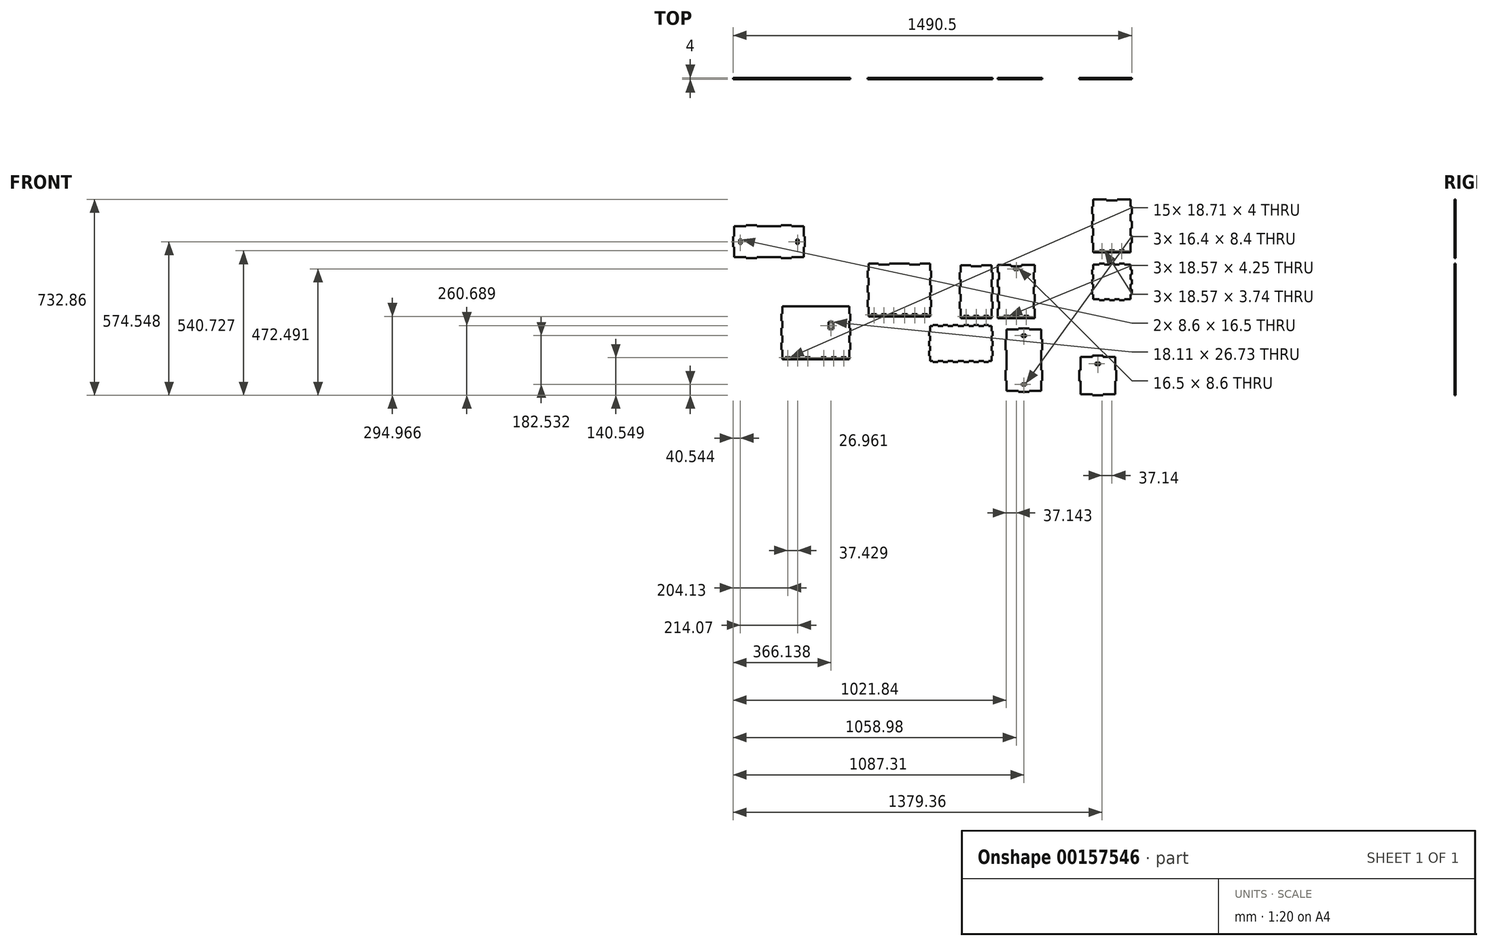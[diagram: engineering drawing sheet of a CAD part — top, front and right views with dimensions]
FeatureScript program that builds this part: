
annotation { "Feature Type Name" : "Feature", "Feature Type Description" : "" }
export const myFeature = defineFeature(function(context is Context, id is Id, definition is map)
    precondition{}
    {
        {
            var Q0;
            Q0=qCreatedBy(makeId("Front.planeOp"),FACE);
            var sketch = newSketch(context, id + "F0", { "sketchPlane" : qUnion([Q0])});
            skLineSegment(sketch, "E0.top", {"start": v(-322.76, -104.52) * mm, "end": v(-304.05, -104.52) * mm});
            skPoint(sketch, "E1.orphan", {"position": v(-191.3, 92.98) * mm});
            skLineSegment(sketch, "E2.0", {"start": v(-322.76, -108.52) * mm, "end": v(-304.05, -108.52) * mm});
            skLineSegment(sketch, "E3.2.0.0", {"start": v(-304.05, -104.52) * mm, "end": v(-304.05, -108.52) * mm});
            skLineSegment(sketch, "E3.3.0.0", {"start": v(-285.34, -104.52) * mm, "end": v(-285.34, -108.52) * mm});
            skLineSegment(sketch, "E3.4.0.0", {"start": v(-266.62, -104.52) * mm, "end": v(-266.62, -108.52) * mm});
            skLineSegment(sketch, "E3.5.0.0", {"start": v(-247.9, -104.52) * mm, "end": v(-247.9, -108.52) * mm});
            skLineSegment(sketch, "E3.6.0.0", {"start": v(-229.2, -104.52) * mm, "end": v(-229.2, -108.52) * mm});
            skLineSegment(sketch, "E4.trimOffspring", {"start": v(-285.34, -104.52) * mm, "end": v(-266.62, -104.52) * mm});
            skLineSegment(sketch, "E5.trimOffspring", {"start": v(-285.34, -108.52) * mm, "end": v(-266.62, -108.52) * mm});
            skLineSegment(sketch, "E6.trimOffspring", {"start": v(-247.9, -104.52) * mm, "end": v(-229.2, -104.52) * mm});
            skLineSegment(sketch, "E7.trimOffspring", {"start": v(-247.9, -108.52) * mm, "end": v(-229.2, -108.52) * mm});
            skLineSegment(sketch, "E8", {"start": v(-322.76, -108.52) * mm, "end": v(-322.76, -104.52) * mm});
            skLineSegment(sketch, "E9.1.0.0", {"start": v(-172.4, -104.27) * mm, "end": v(-172.4, -108.52) * mm});
            skLineSegment(sketch, "E9.2.0.0", {"start": v(-153.84, -104.27) * mm, "end": v(-153.84, -108.52) * mm});
            skLineSegment(sketch, "E9.3.0.0", {"start": v(-135.27, -104.27) * mm, "end": v(-135.27, -108.52) * mm});
            skLineSegment(sketch, "E9.4.0.0", {"start": v(-116.7, -104.27) * mm, "end": v(-116.7, -108.52) * mm});
            skLineSegment(sketch, "E9.5.0.0", {"start": v(-98.12, -104.27) * mm, "end": v(-98.12, -108.52) * mm});
            skLineSegment(sketch, "E9.6.0.0", {"start": v(-79.55, -104.27) * mm, "end": v(-79.55, -108.52) * mm});
            skLineSegment(sketch, "E10", {"start": v(-172.4, -108.52) * mm, "end": v(-153.84, -108.52) * mm});
            skLineSegment(sketch, "E11", {"start": v(-172.4, -104.27) * mm, "end": v(-153.84, -104.27) * mm});
            skPoint(sketch, "E12.orphan", {"position": v(-190.98, -108.52) * mm});
            skLineSegment(sketch, "E13.trimOffspring", {"start": v(-135.27, -104.27) * mm, "end": v(-116.7, -104.27) * mm});
            skLineSegment(sketch, "E14.trimOffspring", {"start": v(-135.27, -108.52) * mm, "end": v(-116.7, -108.52) * mm});
            skLineSegment(sketch, "E15.trimOffspring", {"start": v(-98.12, -104.27) * mm, "end": v(-79.55, -104.27) * mm});
            skLineSegment(sketch, "E16.trimOffspring", {"start": v(-98.12, -108.52) * mm, "end": v(-79.55, -108.52) * mm});
            skPoint(sketch, "E17.orphan", {"position": v(-190.98, -104.27) * mm});
            skPoint(sketch, "E18.orphan", {"position": v(-153.84, -112.52) * mm});
            skPoint(sketch, "E19.orphan", {"position": v(-135.27, -112.52) * mm});
            skPoint(sketch, "E20.orphan", {"position": v(-116.7, -112.52) * mm});
            skPoint(sketch, "E21.orphan", {"position": v(-98.12, -112.52) * mm});
            skPoint(sketch, "E22.orphan", {"position": v(-79.55, -112.52) * mm});
            skLineSegment(sketch, "E23.top", {"start": v(-322.76, -138.52) * mm, "end": v(-304.05, -138.52) * mm});
            skLineSegment(sketch, "E24.2.0.0", {"start": v(-304.05, -138.52) * mm, "end": v(-304.05, -142.52) * mm});
            skLineSegment(sketch, "E24.3.0.0", {"start": v(-285.34, -138.52) * mm, "end": v(-285.34, -142.52) * mm});
            skLineSegment(sketch, "E24.4.0.0", {"start": v(-266.62, -138.52) * mm, "end": v(-266.62, -142.52) * mm});
            skLineSegment(sketch, "E24.5.0.0", {"start": v(-247.9, -138.52) * mm, "end": v(-247.9, -142.52) * mm});
            skLineSegment(sketch, "E24.6.0.0", {"start": v(-229.2, -138.52) * mm, "end": v(-229.2, -142.52) * mm});
            skLineSegment(sketch, "E25.trimOffspring", {"start": v(-285.34, -138.52) * mm, "end": v(-266.62, -138.52) * mm});
            skLineSegment(sketch, "E26.trimOffspring", {"start": v(-247.9, -138.52) * mm, "end": v(-229.2, -138.52) * mm});
            skLineSegment(sketch, "E27", {"start": v(-322.76, -142.52) * mm, "end": v(-322.76, -138.52) * mm});
            skLineSegment(sketch, "E28", {"start": v(-304.05, -142.52) * mm, "end": v(-285.34, -142.52) * mm});
            skLineSegment(sketch, "E29", {"start": v(-266.62, -142.52) * mm, "end": v(-247.9, -142.52) * mm});
            skLineSegment(sketch, "E30", {"start": v(-229.2, -142.52) * mm, "end": v(-218.48, -142.4) * mm});
            skLineSegment(sketch, "E31", {"start": v(-322.76, -142.52) * mm, "end": v(-333.48, -142.52) * mm});
            skPoint(sketch, "E32.orphan", {"position": v(-210.48, -131.68) * mm});
            skLineSegment(sketch, "E33", {"start": v(-218.48, -142.4) * mm, "end": v(-218.48, -161.1) * mm});
            skLineSegment(sketch, "E34.MirrorCS", {"start": v(-266.62, -276.52) * mm, "end": v(-266.62, -272.52) * mm});
            skLineSegment(sketch, "E35.MirrorCS", {"start": v(-247.9, -276.52) * mm, "end": v(-247.9, -272.52) * mm});
            skLineSegment(sketch, "E36.MirrorCS", {"start": v(-229.2, -276.52) * mm, "end": v(-229.2, -272.52) * mm});
            skLineSegment(sketch, "E37.MirrorCS", {"start": v(-322.76, -272.52) * mm, "end": v(-322.76, -276.52) * mm});
            skLineSegment(sketch, "E38.MirrorCS", {"start": v(-285.34, -276.52) * mm, "end": v(-285.34, -272.52) * mm});
            skLineSegment(sketch, "E39.MirrorCS", {"start": v(-304.05, -276.52) * mm, "end": v(-304.05, -272.52) * mm});
            skLineSegment(sketch, "E40.MirrorCS", {"start": v(-322.76, -272.52) * mm, "end": v(-333.48, -272.52) * mm});
            skLineSegment(sketch, "E41.MirrorCS", {"start": v(-285.34, -276.52) * mm, "end": v(-266.62, -276.52) * mm});
            skPoint(sketch, "E42.MirrorP", {"position": v(-210.48, -283.36) * mm});
            skLineSegment(sketch, "E43.MirrorCS", {"start": v(-247.9, -276.52) * mm, "end": v(-229.2, -276.52) * mm});
            skLineSegment(sketch, "E44.MirrorCS", {"start": v(-322.76, -276.52) * mm, "end": v(-304.05, -276.52) * mm});
            skLineSegment(sketch, "E45.MirrorCS", {"start": v(-266.62, -272.52) * mm, "end": v(-247.9, -272.52) * mm});
            skLineSegment(sketch, "E46.MirrorCS", {"start": v(-304.05, -272.52) * mm, "end": v(-285.34, -272.52) * mm});
            skPoint(sketch, "E47.orphan", {"position": v(-218.48, -129.29) * mm});
            skPoint(sketch, "E48.orphan", {"position": v(-210.48, -142.32) * mm});
            skLineSegment(sketch, "E49", {"start": v(-218.48, -161.1) * mm, "end": v(-214.48, -161.1) * mm});
            skLineSegment(sketch, "E50", {"start": v(-229.2, -272.52) * mm, "end": v(-218.48, -272.63) * mm});
            skLineSegment(sketch, "E51.1.0.0", {"start": v(-337.64, 58.34) * mm, "end": v(-333.64, 58.34) * mm});
            skLineSegment(sketch, "E51.2.0.0", {"start": v(-337.64, 31.2) * mm, "end": v(-333.64, 31.2) * mm});
            skLineSegment(sketch, "E51.3.0.0", {"start": v(-337.64, 4.06) * mm, "end": v(-333.64, 4.06) * mm});
            skLineSegment(sketch, "E51.4.0.0", {"start": v(-337.64, -23.09) * mm, "end": v(-333.64, -23.09) * mm});
            skLineSegment(sketch, "E51.5.0.0", {"start": v(-337.64, -50.23) * mm, "end": v(-333.64, -50.23) * mm});
            skLineSegment(sketch, "E51.6.0.0", {"start": v(-337.64, -77.37) * mm, "end": v(-333.64, -77.37) * mm});
            skLineSegment(sketch, "E52", {"start": v(-195.52, 58.34) * mm, "end": v(-190.98, 58.34) * mm});
            skPoint(sketch, "E53.endSnap0", {"position": v(-163.12, -104.27) * mm});
            skLineSegment(sketch, "E54.left", {"start": v(-190.98, 58.34) * mm, "end": v(-190.98, 31.2) * mm});
            skLineSegment(sketch, "E55", {"start": v(-195.52, 85.73) * mm, "end": v(-195.52, 58.34) * mm});
            skLineSegment(sketch, "E56.trimOffspring", {"start": v(-195.52, 31.2) * mm, "end": v(-195.52, 4.06) * mm});
            skLineSegment(sketch, "E57.trimOffspring", {"start": v(-195.52, -23.09) * mm, "end": v(-195.52, -50.23) * mm});
            skLineSegment(sketch, "E58.trimOffspring", {"start": v(-195.52, 4.06) * mm, "end": v(-190.98, 4.06) * mm});
            skLineSegment(sketch, "E59.trimOffspring", {"start": v(-195.52, 31.2) * mm, "end": v(-190.98, 31.2) * mm});
            skLineSegment(sketch, "E60.trimOffspring", {"start": v(-195.52, -23.09) * mm, "end": v(-190.98, -23.09) * mm});
            skLineSegment(sketch, "E61.trimOffspring", {"start": v(-195.52, -50.23) * mm, "end": v(-190.98, -50.23) * mm});
            skLineSegment(sketch, "E62.trimOffspring", {"start": v(-195.52, -77.37) * mm, "end": v(-190.98, -77.37) * mm});
            skLineSegment(sketch, "E63.trimOffspring", {"start": v(-195.52, -77.37) * mm, "end": v(-195.52, -112.52) * mm});
            skLineSegment(sketch, "E64", {"start": v(-190.98, -104.27) * mm, "end": v(-190.98, -104.44) * mm});
            skPoint(sketch, "E65.orphan", {"position": v(-180.53, -104.27) * mm});
            skLineSegment(sketch, "E66.trimOffspring", {"start": v(-190.98, 4.06) * mm, "end": v(-190.98, -23.09) * mm});
            skLineSegment(sketch, "E67.trimOffspring", {"start": v(-190.98, -50.23) * mm, "end": v(-190.98, -77.37) * mm});
            skLineSegment(sketch, "E68.0", {"start": v(-333.64, 85.48) * mm, "end": v(-333.64, 58.34) * mm});
            skLineSegment(sketch, "E69.trimOffspring", {"start": v(-333.64, 31.2) * mm, "end": v(-333.64, 4.06) * mm});
            skLineSegment(sketch, "E70.trimOffspring", {"start": v(-333.64, 85.48) * mm, "end": v(-296.14, 85.48) * mm});
            skLineSegment(sketch, "E71.trimOffspring", {"start": v(-333.64, -23.09) * mm, "end": v(-333.64, -50.23) * mm});
            skLineSegment(sketch, "E72.trimOffspring", {"start": v(-333.64, -77.37) * mm, "end": v(-333.64, -112.52) * mm});
            skLineSegment(sketch, "E73.trimOffspring", {"start": v(-333.64, -112.52) * mm, "end": v(-218.64, -112.52) * mm});
            skLineSegment(sketch, "E74", {"start": v(-337.64, -77.37) * mm, "end": v(-337.64, -50.23) * mm});
            skLineSegment(sketch, "E75", {"start": v(-337.64, -23.09) * mm, "end": v(-337.64, 4.06) * mm});
            skLineSegment(sketch, "E76", {"start": v(-337.64, 31.2) * mm, "end": v(-337.64, 58.34) * mm});
            skLineSegment(sketch, "E77.MirrorCS", {"start": v(-214.64, 58.34) * mm, "end": v(-218.64, 58.34) * mm});
            skLineSegment(sketch, "E78.MirrorCS", {"start": v(-214.64, -50.23) * mm, "end": v(-218.64, -50.23) * mm});
            skLineSegment(sketch, "E79.MirrorCS", {"start": v(-214.64, 31.2) * mm, "end": v(-218.64, 31.2) * mm});
            skLineSegment(sketch, "E80.MirrorCS", {"start": v(-214.64, -77.37) * mm, "end": v(-218.64, -77.37) * mm});
            skLineSegment(sketch, "E81.MirrorCS", {"start": v(-214.64, -23.09) * mm, "end": v(-218.64, -23.09) * mm});
            skLineSegment(sketch, "E82.MirrorCS", {"start": v(-214.64, 4.06) * mm, "end": v(-218.64, 4.06) * mm});
            skPoint(sketch, "E83.MirrorP", {"position": v(-211.02, 4.06) * mm});
            skLineSegment(sketch, "E84.MirrorCS", {"start": v(-214.64, -23.09) * mm, "end": v(-214.64, 4.06) * mm});
            skLineSegment(sketch, "E85.MirrorCS", {"start": v(-214.64, -77.37) * mm, "end": v(-214.64, -50.23) * mm});
            skLineSegment(sketch, "E86.MirrorCS", {"start": v(-218.64, -77.37) * mm, "end": v(-218.64, -112.52) * mm});
            skLineSegment(sketch, "E87.MirrorCS", {"start": v(-218.64, -23.09) * mm, "end": v(-218.64, -50.23) * mm});
            skLineSegment(sketch, "E88.MirrorCS", {"start": v(-214.64, 31.2) * mm, "end": v(-214.64, 58.34) * mm});
            skPoint(sketch, "E89.MirrorP", {"position": v(-211.56, -77.37) * mm});
            skPoint(sketch, "E90.MirrorP", {"position": v(-211.38, -50.23) * mm});
            skPoint(sketch, "E91.MirrorP", {"position": v(-211.2, -23.09) * mm});
            skLineSegment(sketch, "E92.MirrorCS", {"start": v(-218.64, 31.2) * mm, "end": v(-218.64, 4.06) * mm});
            skLineSegment(sketch, "E93.MirrorCS", {"start": v(-218.64, 85.48) * mm, "end": v(-218.64, 58.34) * mm});
            skPoint(sketch, "E94.MirrorP", {"position": v(-210.84, 31.2) * mm});
            skPoint(sketch, "E95.orphan", {"position": v(-210.64, -112.52) * mm});
            skPoint(sketch, "E96.MirrorP", {"position": v(-75.98, -104.27) * mm});
            skLineSegment(sketch, "E97.1.0.0", {"start": v(-218.48, -179.67) * mm, "end": v(-214.48, -179.67) * mm});
            skLineSegment(sketch, "E97.2.0.0", {"start": v(-218.48, -198.24) * mm, "end": v(-214.48, -198.24) * mm});
            skLineSegment(sketch, "E97.3.0.0", {"start": v(-218.48, -216.8) * mm, "end": v(-214.48, -216.81) * mm});
            skLineSegment(sketch, "E97.4.0.0", {"start": v(-218.48, -235.38) * mm, "end": v(-214.48, -235.38) * mm});
            skLineSegment(sketch, "E97.5.0.0", {"start": v(-218.48, -253.95) * mm, "end": v(-214.48, -253.95) * mm});
            skLineSegment(sketch, "E97.6.0.0", {"start": v(-229.99, -272.52) * mm, "end": v(-218.48, -272.52) * mm, "construction": true});
            skLineSegment(sketch, "E98", {"start": v(-214.48, -161.1) * mm, "end": v(-214.48, -179.67) * mm});
            skLineSegment(sketch, "E99.trimOffspring", {"start": v(-214.48, -198.24) * mm, "end": v(-214.48, -216.81) * mm});
            skLineSegment(sketch, "E100.trimOffspring", {"start": v(-214.48, -235.38) * mm, "end": v(-214.48, -253.95) * mm});
            skPoint(sketch, "E101.orphan", {"position": v(-190.56, -272.54) * mm});
            skLineSegment(sketch, "E102.trimOffspring", {"start": v(-218.48, -179.67) * mm, "end": v(-218.48, -198.24) * mm});
            skLineSegment(sketch, "E103.trimOffspring", {"start": v(-218.48, -216.8) * mm, "end": v(-218.48, -235.38) * mm});
            skLineSegment(sketch, "E104.trimOffspring", {"start": v(-218.48, -253.95) * mm, "end": v(-218.48, -272.63) * mm});
            skPoint(sketch, "E105.orphan", {"position": v(-229.73, -235.37) * mm});
            skPoint(sketch, "E106.orphan", {"position": v(-229.86, -253.94) * mm});
            skPoint(sketch, "E107.orphan", {"position": v(-229.6, -216.8) * mm});
            skPoint(sketch, "E108.orphan", {"position": v(-229.46, -198.23) * mm});
            skPoint(sketch, "E109.orphan", {"position": v(-189.78, -161.11) * mm});
            skPoint(sketch, "E110.orphan", {"position": v(-189.91, -179.68) * mm});
            skPoint(sketch, "E111.orphan", {"position": v(-190.04, -198.26) * mm});
            skPoint(sketch, "E112.orphan", {"position": v(-190.17, -216.83) * mm});
            skPoint(sketch, "E113.orphan", {"position": v(-190.3, -235.4) * mm});
            skPoint(sketch, "E114.orphan", {"position": v(-190.43, -253.97) * mm});
            skPoint(sketch, "E115.MirrorP", {"position": v(-341.48, -142.32) * mm});
            skPoint(sketch, "E116.MirrorP", {"position": v(-341.48, -283.36) * mm});
            skPoint(sketch, "E117.MirrorP", {"position": v(-341.48, -131.68) * mm});
            skPoint(sketch, "E118.MirrorP", {"position": v(-333.48, -129.29) * mm});
            skLineSegment(sketch, "E119.MirrorCS", {"start": v(-60.98, -104.27) * mm, "end": v(-60.98, -104.44) * mm});
            skLineSegment(sketch, "E120.MirrorCS", {"start": v(-56.44, 31.2) * mm, "end": v(-60.98, 31.2) * mm});
            skLineSegment(sketch, "E121.MirrorCS", {"start": v(-56.44, -77.37) * mm, "end": v(-60.98, -77.37) * mm});
            skLineSegment(sketch, "E122.MirrorCS", {"start": v(-56.44, -23.09) * mm, "end": v(-60.98, -23.09) * mm});
            skLineSegment(sketch, "E123.MirrorCS", {"start": v(-56.44, 58.34) * mm, "end": v(-60.98, 58.34) * mm});
            skLineSegment(sketch, "E124.MirrorCS", {"start": v(-56.44, 4.06) * mm, "end": v(-60.98, 4.06) * mm});
            skLineSegment(sketch, "E125.MirrorCS", {"start": v(-56.44, -50.23) * mm, "end": v(-60.98, -50.23) * mm});
            skPoint(sketch, "E126.MirrorP", {"position": v(-60.98, 92.98) * mm});
            skLineSegment(sketch, "E127.MirrorCS", {"start": v(-56.44, -77.37) * mm, "end": v(-56.44, -112.52) * mm});
            skPoint(sketch, "E128.MirrorP", {"position": v(-60.98, -108.52) * mm});
            skPoint(sketch, "E129.MirrorP", {"position": v(-60.98, -104.27) * mm});
            skLineSegment(sketch, "E130.MirrorCS", {"start": v(-60.98, 4.06) * mm, "end": v(-60.98, -23.09) * mm});
            skPoint(sketch, "E131.MirrorP", {"position": v(-71.43, -104.27) * mm});
            skLineSegment(sketch, "E132.MirrorCS", {"start": v(-60.98, -50.23) * mm, "end": v(-60.98, -77.37) * mm});
            skLineSegment(sketch, "E133.MirrorCS", {"start": v(-60.98, 58.34) * mm, "end": v(-60.98, 31.2) * mm});
            skLineSegment(sketch, "E134.MirrorCS", {"start": v(-56.44, 31.2) * mm, "end": v(-56.44, 4.06) * mm});
            skLineSegment(sketch, "E135.MirrorCS", {"start": v(-56.44, -23.09) * mm, "end": v(-56.44, -50.23) * mm});
            skLineSegment(sketch, "E136.MirrorCS", {"start": v(-56.44, 85.73) * mm, "end": v(-56.44, 58.34) * mm});
            skLineSegment(sketch, "E137", {"start": v(-195.52, 85.73) * mm, "end": v(-145.98, 85.73) * mm});
            skLineSegment(sketch, "E138", {"start": v(-195.52, -112.52) * mm, "end": v(-56.44, -112.52) * mm});
            skLineSegment(sketch, "E139.top", {"start": v(-296.14, 81.48) * mm, "end": v(-256.14, 81.48) * mm});
            skLineSegment(sketch, "E139.left", {"start": v(-296.14, 85.48) * mm, "end": v(-296.14, 81.48) * mm});
            skLineSegment(sketch, "E139.right", {"start": v(-256.14, 85.48) * mm, "end": v(-256.14, 81.48) * mm});
            skLineSegment(sketch, "E140.top", {"start": v(-145.98, 81.73) * mm, "end": v(-105.98, 81.73) * mm});
            skLineSegment(sketch, "E140.left", {"start": v(-145.98, 85.73) * mm, "end": v(-145.98, 81.73) * mm});
            skLineSegment(sketch, "E140.right", {"start": v(-105.98, 85.73) * mm, "end": v(-105.98, 81.73) * mm});
            skLineSegment(sketch, "E141.trimOffspring", {"start": v(-256.14, 85.48) * mm, "end": v(-218.64, 85.48) * mm});
            skPoint(sketch, "E142.orphan", {"position": v(-296.14, 92.98) * mm});
            skLineSegment(sketch, "E143.trimOffspring", {"start": v(-105.98, 85.73) * mm, "end": v(-56.44, 85.73) * mm});
            skLineSegment(sketch, "E144.bottom", {"start": v(-162.65, -154.55) * mm, "end": v(-117.65, -154.55) * mm});
            skLineSegment(sketch, "E144.left", {"start": v(-162.65, -154.55) * mm, "end": v(-162.65, -192.05) * mm});
            skLineSegment(sketch, "E144.right", {"start": v(-32.65, -154.55) * mm, "end": v(-32.65, -192.05) * mm});
            skLineSegment(sketch, "E145.bottom", {"start": v(-162.65, -192.05) * mm, "end": v(-166.65, -192.05) * mm});
            skLineSegment(sketch, "E145.top", {"start": v(-162.65, -232.05) * mm, "end": v(-166.65, -232.05) * mm});
            skLineSegment(sketch, "E145.right", {"start": v(-166.65, -192.05) * mm, "end": v(-166.65, -232.05) * mm});
            skLineSegment(sketch, "E146.bottom", {"start": v(-117.65, -150.55) * mm, "end": v(-77.65, -150.55) * mm});
            skLineSegment(sketch, "E146.left", {"start": v(-117.65, -150.55) * mm, "end": v(-117.65, -154.55) * mm});
            skLineSegment(sketch, "E146.right", {"start": v(-77.65, -150.55) * mm, "end": v(-77.65, -154.55) * mm});
            skLineSegment(sketch, "E147.trimOffspring", {"start": v(-162.65, -232.05) * mm, "end": v(-162.65, -269.55) * mm});
            skLineSegment(sketch, "E148.trimOffspring", {"start": v(-77.65, -154.55) * mm, "end": v(-32.65, -154.55) * mm});
            skLineSegment(sketch, "E149.MirrorCS", {"start": v(-32.65, -232.05) * mm, "end": v(-28.65, -232.05) * mm});
            skLineSegment(sketch, "E150.MirrorCS", {"start": v(-28.65, -192.05) * mm, "end": v(-28.65, -232.05) * mm});
            skLineSegment(sketch, "E151.MirrorCS", {"start": v(-32.65, -192.05) * mm, "end": v(-28.65, -192.05) * mm});
            skLineSegment(sketch, "E152.trimOffspring", {"start": v(-32.65, -232.05) * mm, "end": v(-32.65, -269.55) * mm});
            skLineSegment(sketch, "E153.MirrorCS", {"start": v(-437.76, -142.52) * mm, "end": v(-448.48, -142.4) * mm});
            skLineSegment(sketch, "E154.MirrorCS", {"start": v(-362.9, -138.52) * mm, "end": v(-362.9, -142.52) * mm});
            skLineSegment(sketch, "E155.MirrorCS", {"start": v(-437.76, -138.52) * mm, "end": v(-437.76, -142.52) * mm});
            skLineSegment(sketch, "E156.MirrorCS", {"start": v(-381.62, -138.52) * mm, "end": v(-381.62, -142.52) * mm});
            skLineSegment(sketch, "E157.MirrorCS", {"start": v(-400.34, -138.52) * mm, "end": v(-400.34, -142.52) * mm});
            skLineSegment(sketch, "E158.MirrorCS", {"start": v(-419.05, -138.52) * mm, "end": v(-419.05, -142.52) * mm});
            skLineSegment(sketch, "E159.MirrorCS", {"start": v(-344.2, -142.52) * mm, "end": v(-344.2, -138.52) * mm});
            skLineSegment(sketch, "E160.MirrorCS", {"start": v(-362.9, -142.52) * mm, "end": v(-381.62, -142.52) * mm});
            skPoint(sketch, "E161.MirrorP", {"position": v(-456.48, -142.32) * mm});
            skLineSegment(sketch, "E162.MirrorCS", {"start": v(-400.34, -142.52) * mm, "end": v(-419.05, -142.52) * mm});
            skLineSegment(sketch, "E163.MirrorCS", {"start": v(-419.05, -138.52) * mm, "end": v(-437.76, -138.52) * mm});
            skPoint(sketch, "E164.MirrorP", {"position": v(-456.48, -131.68) * mm});
            skLineSegment(sketch, "E165.MirrorCS", {"start": v(-344.2, -138.52) * mm, "end": v(-362.9, -138.52) * mm});
            skLineSegment(sketch, "E166.MirrorCS", {"start": v(-381.62, -138.52) * mm, "end": v(-400.34, -138.52) * mm});
            skLineSegment(sketch, "E167.MirrorCS", {"start": v(-437.76, -276.52) * mm, "end": v(-437.76, -272.52) * mm});
            skLineSegment(sketch, "E168.MirrorCS", {"start": v(-344.2, -272.52) * mm, "end": v(-344.2, -276.52) * mm});
            skLineSegment(sketch, "E169.MirrorCS", {"start": v(-419.05, -276.52) * mm, "end": v(-419.05, -272.52) * mm});
            skLineSegment(sketch, "E170.MirrorCS", {"start": v(-400.34, -276.52) * mm, "end": v(-400.34, -272.52) * mm});
            skLineSegment(sketch, "E171.MirrorCS", {"start": v(-381.62, -276.52) * mm, "end": v(-381.62, -272.52) * mm});
            skLineSegment(sketch, "E172.MirrorCS", {"start": v(-362.9, -276.52) * mm, "end": v(-362.9, -272.52) * mm});
            skPoint(sketch, "E173.MirrorP", {"position": v(-437.1, -253.94) * mm});
            skLineSegment(sketch, "E174.MirrorCS", {"start": v(-381.62, -276.52) * mm, "end": v(-400.34, -276.52) * mm});
            skLineSegment(sketch, "E175.MirrorCS", {"start": v(-344.2, -276.52) * mm, "end": v(-362.9, -276.52) * mm});
            skLineSegment(sketch, "E176.MirrorCS", {"start": v(-400.34, -272.52) * mm, "end": v(-419.05, -272.52) * mm});
            skLineSegment(sketch, "E177.MirrorCS", {"start": v(-362.9, -272.52) * mm, "end": v(-381.62, -272.52) * mm});
            skLineSegment(sketch, "E178.MirrorCS", {"start": v(-419.05, -276.52) * mm, "end": v(-437.76, -276.52) * mm});
            skLineSegment(sketch, "E179.MirrorCS", {"start": v(-448.48, -235.38) * mm, "end": v(-452.48, -235.38) * mm});
            skLineSegment(sketch, "E180.MirrorCS", {"start": v(-448.48, -179.67) * mm, "end": v(-452.48, -179.67) * mm});
            skLineSegment(sketch, "E181.MirrorCS", {"start": v(-448.48, -216.8) * mm, "end": v(-452.48, -216.81) * mm});
            skLineSegment(sketch, "E182.MirrorCS", {"start": v(-448.48, -161.1) * mm, "end": v(-452.48, -161.1) * mm});
            skLineSegment(sketch, "E183.MirrorCS", {"start": v(-448.48, -253.95) * mm, "end": v(-452.48, -253.95) * mm});
            skLineSegment(sketch, "E184.MirrorCS", {"start": v(-448.48, -198.24) * mm, "end": v(-452.48, -198.24) * mm});
            skLineSegment(sketch, "E185.MirrorCS", {"start": v(-448.48, -179.67) * mm, "end": v(-448.48, -198.24) * mm});
            skPoint(sketch, "E186.MirrorP", {"position": v(-437.23, -235.37) * mm});
            skLineSegment(sketch, "E187.MirrorCS", {"start": v(-448.48, -216.8) * mm, "end": v(-448.48, -235.38) * mm});
            skLineSegment(sketch, "E188.MirrorCS", {"start": v(-452.48, -235.38) * mm, "end": v(-452.48, -253.95) * mm});
            skLineSegment(sketch, "E189.MirrorCS", {"start": v(-448.48, -253.95) * mm, "end": v(-448.48, -272.63) * mm});
            skLineSegment(sketch, "E190.MirrorCS", {"start": v(-452.48, -198.24) * mm, "end": v(-452.48, -216.81) * mm});
            skPoint(sketch, "E191.MirrorP", {"position": v(-448.48, -129.29) * mm});
            skLineSegment(sketch, "E192.MirrorCS", {"start": v(-452.48, -161.1) * mm, "end": v(-452.48, -179.67) * mm});
            skLineSegment(sketch, "E193.MirrorCS", {"start": v(-448.48, -142.4) * mm, "end": v(-448.48, -161.1) * mm});
            skPoint(sketch, "E194.MirrorP", {"position": v(-437.5, -198.23) * mm});
            skPoint(sketch, "E195.MirrorP", {"position": v(-456.48, -283.36) * mm});
            skPoint(sketch, "E196.MirrorP", {"position": v(-437.36, -216.8) * mm});
            skLineSegment(sketch, "E197", {"start": v(-448.48, -272.63) * mm, "end": v(-437.76, -272.52) * mm});
            skLineSegment(sketch, "E198", {"start": v(-344.2, -142.52) * mm, "end": v(-333.48, -142.52) * mm});
            skLineSegment(sketch, "E199", {"start": v(-344.2, -272.52) * mm, "end": v(-333.48, -272.52) * mm});
            skLineSegment(sketch, "E200.top", {"start": v(-990.19, -258.81) * mm, "end": v(-971.47, -258.81) * mm});
            skLineSegment(sketch, "E201.0", {"start": v(-990.19, -262.81) * mm, "end": v(-971.47, -262.81) * mm});
            skLineSegment(sketch, "E202.2.0.0", {"start": v(-971.47, -258.81) * mm, "end": v(-971.47, -262.81) * mm});
            skLineSegment(sketch, "E202.3.0.0", {"start": v(-952.76, -258.81) * mm, "end": v(-952.76, -262.81) * mm});
            skLineSegment(sketch, "E202.4.0.0", {"start": v(-934.04, -258.81) * mm, "end": v(-934.04, -262.81) * mm});
            skLineSegment(sketch, "E202.5.0.0", {"start": v(-915.33, -258.81) * mm, "end": v(-915.33, -262.81) * mm});
            skLineSegment(sketch, "E202.6.0.0", {"start": v(-896.62, -258.81) * mm, "end": v(-896.62, -262.81) * mm});
            skLineSegment(sketch, "E203.trimOffspring", {"start": v(-952.76, -258.81) * mm, "end": v(-934.04, -258.81) * mm});
            skLineSegment(sketch, "E204.trimOffspring", {"start": v(-952.76, -262.81) * mm, "end": v(-934.04, -262.81) * mm});
            skLineSegment(sketch, "E205.trimOffspring", {"start": v(-915.33, -258.81) * mm, "end": v(-896.62, -258.81) * mm});
            skLineSegment(sketch, "E206.trimOffspring", {"start": v(-915.33, -262.81) * mm, "end": v(-896.62, -262.81) * mm});
            skLineSegment(sketch, "E207", {"start": v(-990.19, -262.81) * mm, "end": v(-990.19, -258.81) * mm});
            skLineSegment(sketch, "E208.1.0.0", {"start": v(-1005.06, -95.95) * mm, "end": v(-1001.06, -95.95) * mm});
            skLineSegment(sketch, "E208.2.0.0", {"start": v(-1005.06, -123.1) * mm, "end": v(-1001.06, -123.1) * mm});
            skLineSegment(sketch, "E208.3.0.0", {"start": v(-1005.06, -150.24) * mm, "end": v(-1001.06, -150.24) * mm});
            skLineSegment(sketch, "E208.4.0.0", {"start": v(-1005.06, -177.38) * mm, "end": v(-1001.06, -177.38) * mm});
            skLineSegment(sketch, "E208.5.0.0", {"start": v(-1005.06, -204.52) * mm, "end": v(-1001.06, -204.52) * mm});
            skLineSegment(sketch, "E208.6.0.0", {"start": v(-1005.06, -231.66) * mm, "end": v(-1001.06, -231.66) * mm});
            skLineSegment(sketch, "E209.0", {"start": v(-1001.06, -68.81) * mm, "end": v(-1001.06, -95.95) * mm});
            skLineSegment(sketch, "E210.trimOffspring", {"start": v(-1001.06, -123.1) * mm, "end": v(-1001.06, -150.24) * mm});
            skLineSegment(sketch, "E211.trimOffspring", {"start": v(-1001.06, -68.81) * mm, "end": v(-963.56, -68.81) * mm});
            skLineSegment(sketch, "E212.trimOffspring", {"start": v(-1001.06, -177.38) * mm, "end": v(-1001.06, -204.52) * mm});
            skLineSegment(sketch, "E213.trimOffspring", {"start": v(-1001.06, -231.66) * mm, "end": v(-1001.06, -266.81) * mm});
            skLineSegment(sketch, "E214", {"start": v(-1005.06, -231.66) * mm, "end": v(-1005.06, -204.52) * mm});
            skLineSegment(sketch, "E215", {"start": v(-1005.06, -177.38) * mm, "end": v(-1005.06, -150.24) * mm});
            skLineSegment(sketch, "E216", {"start": v(-1005.06, -123.1) * mm, "end": v(-1005.06, -95.95) * mm});
            skLineSegment(sketch, "E217.top", {"start": v(-963.56, -72.81) * mm, "end": v(-923.56, -72.81) * mm});
            skLineSegment(sketch, "E217.left", {"start": v(-963.56, -68.81) * mm, "end": v(-963.56, -72.81) * mm});
            skLineSegment(sketch, "E217.right", {"start": v(-923.56, -68.81) * mm, "end": v(-923.56, -72.81) * mm});
            skLineSegment(sketch, "E218.trimOffspring", {"start": v(-923.56, -68.81) * mm, "end": v(-886.06, -68.81) * mm});
            skPoint(sketch, "E219.orphan", {"position": v(-963.56, -61.32) * mm});
            skLineSegment(sketch, "E220", {"start": v(-1001.06, -68.81) * mm, "end": v(-751.06, -68.81) * mm});
            skLineSegment(sketch, "E221", {"start": v(-876.06, -45.03) * mm, "end": v(-876.06, -302.96) * mm, "construction": true});
            skLineSegment(sketch, "E222.MirrorCS", {"start": v(-751.06, -68.81) * mm, "end": v(-751.06, -95.95) * mm});
            skLineSegment(sketch, "E223.MirrorCS", {"start": v(-818.08, -258.81) * mm, "end": v(-818.08, -262.81) * mm});
            skLineSegment(sketch, "E224.MirrorCS", {"start": v(-780.65, -258.81) * mm, "end": v(-780.65, -262.81) * mm});
            skLineSegment(sketch, "E225.MirrorCS", {"start": v(-855.5, -258.81) * mm, "end": v(-855.5, -262.81) * mm});
            skLineSegment(sketch, "E226.MirrorCS", {"start": v(-747.06, -204.52) * mm, "end": v(-751.06, -204.52) * mm});
            skLineSegment(sketch, "E227.MirrorCS", {"start": v(-836.8, -258.81) * mm, "end": v(-836.8, -262.81) * mm});
            skLineSegment(sketch, "E228.MirrorCS", {"start": v(-747.06, -123.1) * mm, "end": v(-751.06, -123.1) * mm});
            skLineSegment(sketch, "E229.MirrorCS", {"start": v(-747.06, -95.95) * mm, "end": v(-751.06, -95.95) * mm});
            skLineSegment(sketch, "E230.MirrorCS", {"start": v(-761.94, -262.81) * mm, "end": v(-761.94, -258.81) * mm});
            skLineSegment(sketch, "E231.MirrorCS", {"start": v(-799.37, -258.81) * mm, "end": v(-799.37, -262.81) * mm});
            skLineSegment(sketch, "E232.MirrorCS", {"start": v(-747.06, -177.38) * mm, "end": v(-751.06, -177.38) * mm});
            skLineSegment(sketch, "E233.MirrorCS", {"start": v(-747.06, -231.66) * mm, "end": v(-751.06, -231.66) * mm});
            skLineSegment(sketch, "E234.MirrorCS", {"start": v(-747.06, -150.24) * mm, "end": v(-751.06, -150.24) * mm});
            skLineSegment(sketch, "E235.MirrorCS", {"start": v(-799.37, -262.81) * mm, "end": v(-818.08, -262.81) * mm});
            skLineSegment(sketch, "E236.MirrorCS", {"start": v(-799.37, -258.81) * mm, "end": v(-818.08, -258.81) * mm});
            skLineSegment(sketch, "E237.MirrorCS", {"start": v(-836.8, -262.81) * mm, "end": v(-855.5, -262.81) * mm});
            skLineSegment(sketch, "E238.MirrorCS", {"start": v(-751.06, -123.1) * mm, "end": v(-751.06, -150.24) * mm});
            skLineSegment(sketch, "E239.MirrorCS", {"start": v(-761.94, -258.81) * mm, "end": v(-780.65, -258.81) * mm});
            skLineSegment(sketch, "E240.MirrorCS", {"start": v(-751.06, -177.38) * mm, "end": v(-751.06, -204.52) * mm});
            skLineSegment(sketch, "E241.MirrorCS", {"start": v(-747.06, -177.38) * mm, "end": v(-747.06, -150.24) * mm});
            skLineSegment(sketch, "E242.MirrorCS", {"start": v(-836.8, -258.81) * mm, "end": v(-855.5, -258.81) * mm});
            skLineSegment(sketch, "E243.MirrorCS", {"start": v(-747.06, -123.1) * mm, "end": v(-747.06, -95.95) * mm});
            skLineSegment(sketch, "E244.MirrorCS", {"start": v(-747.06, -231.66) * mm, "end": v(-747.06, -204.52) * mm});
            skLineSegment(sketch, "E245.MirrorCS", {"start": v(-761.94, -262.81) * mm, "end": v(-780.65, -262.81) * mm});
            skLineSegment(sketch, "E246.MirrorCS", {"start": v(-751.06, -231.66) * mm, "end": v(-751.06, -266.81) * mm});
            skLineSegment(sketch, "E247", {"start": v(-1001.06, -266.81) * mm, "end": v(-751.06, -266.81) * mm});
            skLineSegment(sketch, "E248.MirrorCS", {"start": v(-788.56, -68.81) * mm, "end": v(-788.56, -72.81) * mm});
            skLineSegment(sketch, "E249.MirrorCS", {"start": v(-788.56, -72.81) * mm, "end": v(-828.56, -72.81) * mm});
            skLineSegment(sketch, "E250.MirrorCS", {"start": v(-828.56, -68.81) * mm, "end": v(-828.56, -72.81) * mm});
            skPoint(sketch, "E251.MirrorP", {"position": v(-816.26, -285.32) * mm});
            skLineSegment(sketch, "E252.top", {"start": v(-552.42, -98.2) * mm, "end": v(-533.7, -98.2) * mm});
            skPoint(sketch, "E253.orphan", {"position": v(-420.95, 99.3) * mm});
            skLineSegment(sketch, "E254.0", {"start": v(-552.42, -102.2) * mm, "end": v(-533.7, -102.2) * mm});
            skLineSegment(sketch, "E255.2.0.0", {"start": v(-533.7, -98.2) * mm, "end": v(-533.7, -102.2) * mm});
            skLineSegment(sketch, "E255.3.0.0", {"start": v(-514.99, -98.2) * mm, "end": v(-514.99, -102.2) * mm});
            skLineSegment(sketch, "E255.4.0.0", {"start": v(-496.27, -98.2) * mm, "end": v(-496.27, -102.2) * mm});
            skLineSegment(sketch, "E255.5.0.0", {"start": v(-477.56, -98.2) * mm, "end": v(-477.56, -102.2) * mm});
            skLineSegment(sketch, "E255.6.0.0", {"start": v(-458.84, -98.2) * mm, "end": v(-458.84, -102.2) * mm});
            skLineSegment(sketch, "E256.trimOffspring", {"start": v(-514.99, -98.2) * mm, "end": v(-496.27, -98.2) * mm});
            skLineSegment(sketch, "E257.trimOffspring", {"start": v(-514.99, -102.2) * mm, "end": v(-496.27, -102.2) * mm});
            skLineSegment(sketch, "E258.trimOffspring", {"start": v(-477.56, -98.2) * mm, "end": v(-458.84, -98.2) * mm});
            skLineSegment(sketch, "E259.trimOffspring", {"start": v(-477.56, -102.2) * mm, "end": v(-458.84, -102.2) * mm});
            skLineSegment(sketch, "E260", {"start": v(-552.42, -102.2) * mm, "end": v(-552.42, -98.2) * mm});
            skPoint(sketch, "E261.orphan", {"position": v(-420.63, -102.2) * mm});
            skPoint(sketch, "E262.orphan", {"position": v(-420.63, -97.95) * mm});
            skPoint(sketch, "E263.orphan", {"position": v(-440.13, -136) * mm});
            skLineSegment(sketch, "E264.trimOffspring", {"start": v(-563.3, 91.8) * mm, "end": v(-525.8, 91.8) * mm});
            skLineSegment(sketch, "E265.trimOffspring", {"start": v(-563.3, -106.2) * mm, "end": v(-448.3, -106.2) * mm});
            skLineSegment(sketch, "E266.MirrorCS", {"start": v(-444.3, 64.66) * mm, "end": v(-448.3, 64.66) * mm});
            skLineSegment(sketch, "E267.MirrorCS", {"start": v(-444.3, -43.9) * mm, "end": v(-448.3, -43.9) * mm});
            skLineSegment(sketch, "E268.MirrorCS", {"start": v(-444.3, 37.52) * mm, "end": v(-448.3, 37.52) * mm});
            skLineSegment(sketch, "E269.MirrorCS", {"start": v(-444.3, -71.05) * mm, "end": v(-448.3, -71.05) * mm});
            skLineSegment(sketch, "E270.MirrorCS", {"start": v(-444.3, -16.77) * mm, "end": v(-448.3, -16.77) * mm});
            skLineSegment(sketch, "E271.MirrorCS", {"start": v(-444.3, 10.38) * mm, "end": v(-448.3, 10.38) * mm});
            skPoint(sketch, "E272.MirrorP", {"position": v(-435, 13.65) * mm});
            skLineSegment(sketch, "E273.MirrorCS", {"start": v(-444.3, -16.77) * mm, "end": v(-444.3, 10.38) * mm});
            skLineSegment(sketch, "E274.MirrorCS", {"start": v(-444.3, -71.05) * mm, "end": v(-444.3, -43.9) * mm});
            skLineSegment(sketch, "E275.MirrorCS", {"start": v(-448.3, -71.05) * mm, "end": v(-448.3, -106.2) * mm});
            skLineSegment(sketch, "E276.MirrorCS", {"start": v(-448.3, -16.77) * mm, "end": v(-448.3, -43.9) * mm});
            skLineSegment(sketch, "E277.MirrorCS", {"start": v(-444.3, 37.52) * mm, "end": v(-444.3, 64.66) * mm});
            skPoint(sketch, "E278.MirrorP", {"position": v(-441.21, -71.05) * mm});
            skPoint(sketch, "E279.MirrorP", {"position": v(-441.03, -43.9) * mm});
            skPoint(sketch, "E280.MirrorP", {"position": v(-440.85, -16.77) * mm});
            skLineSegment(sketch, "E281.MirrorCS", {"start": v(-448.3, 37.52) * mm, "end": v(-448.3, 10.38) * mm});
            skLineSegment(sketch, "E282.MirrorCS", {"start": v(-448.3, 91.8) * mm, "end": v(-448.3, 64.66) * mm});
            skPoint(sketch, "E283.MirrorP", {"position": v(-440.5, 37.52) * mm});
            skPoint(sketch, "E284.orphan", {"position": v(-440.3, -106.2) * mm});
            skPoint(sketch, "E285.MirrorP", {"position": v(-571.13, -136) * mm});
            skLineSegment(sketch, "E286.top", {"start": v(-525.8, 87.8) * mm, "end": v(-485.8, 87.8) * mm});
            skLineSegment(sketch, "E286.left", {"start": v(-525.8, 91.8) * mm, "end": v(-525.8, 87.8) * mm});
            skLineSegment(sketch, "E286.right", {"start": v(-485.8, 91.8) * mm, "end": v(-485.8, 87.8) * mm});
            skLineSegment(sketch, "E287.trimOffspring", {"start": v(-485.8, 91.8) * mm, "end": v(-448.3, 91.8) * mm});
            skPoint(sketch, "E288.orphan", {"position": v(-525.8, 99.3) * mm});
            skLineSegment(sketch, "E289", {"start": v(-563.3, -106.2) * mm, "end": v(-563.3, 91.8) * mm});
            skLineSegment(sketch, "E290.MirrorCS", {"start": v(-682.3, -16.77) * mm, "end": v(-678.3, -16.77) * mm});
            skLineSegment(sketch, "E291.MirrorCS", {"start": v(-682.3, -71.05) * mm, "end": v(-678.3, -71.05) * mm});
            skLineSegment(sketch, "E292.MirrorCS", {"start": v(-682.3, -43.9) * mm, "end": v(-678.3, -43.9) * mm});
            skLineSegment(sketch, "E293.MirrorCS", {"start": v(-682.3, 37.52) * mm, "end": v(-678.3, 37.52) * mm});
            skLineSegment(sketch, "E294.MirrorCS", {"start": v(-682.3, 64.66) * mm, "end": v(-678.3, 64.66) * mm});
            skLineSegment(sketch, "E295.MirrorCS", {"start": v(-682.3, 10.38) * mm, "end": v(-678.3, 10.38) * mm});
            skPoint(sketch, "E296.MirrorP", {"position": v(-686.3, -106.2) * mm});
            skPoint(sketch, "E297.MirrorP", {"position": v(-685.37, -71.05) * mm});
            skLineSegment(sketch, "E298.MirrorCS", {"start": v(-682.3, -16.77) * mm, "end": v(-682.3, 10.38) * mm});
            skLineSegment(sketch, "E299.MirrorCS", {"start": v(-682.3, -71.05) * mm, "end": v(-682.3, -43.9) * mm});
            skPoint(sketch, "E300.MirrorP", {"position": v(-685.55, -43.9) * mm});
            skPoint(sketch, "E301.MirrorP", {"position": v(-686.1, 37.52) * mm});
            skLineSegment(sketch, "E302.MirrorCS", {"start": v(-678.3, -71.05) * mm, "end": v(-678.3, -106.2) * mm});
            skPoint(sketch, "E303.MirrorP", {"position": v(-691.58, 13.65) * mm});
            skLineSegment(sketch, "E304.MirrorCS", {"start": v(-678.3, -16.77) * mm, "end": v(-678.3, -43.9) * mm});
            skLineSegment(sketch, "E305.MirrorCS", {"start": v(-682.3, 37.52) * mm, "end": v(-682.3, 64.66) * mm});
            skPoint(sketch, "E306.MirrorP", {"position": v(-685.73, -16.77) * mm});
            skLineSegment(sketch, "E307.MirrorCS", {"start": v(-678.3, 91.8) * mm, "end": v(-678.3, 64.66) * mm});
            skLineSegment(sketch, "E308.MirrorCS", {"start": v(-678.3, 37.52) * mm, "end": v(-678.3, 10.38) * mm});
            skLineSegment(sketch, "E309.MirrorCS", {"start": v(-640.8, 91.8) * mm, "end": v(-678.3, 91.8) * mm});
            skLineSegment(sketch, "E310.MirrorCS", {"start": v(-563.3, 91.8) * mm, "end": v(-600.8, 91.8) * mm});
            skLineSegment(sketch, "E311.MirrorCS", {"start": v(-600.8, 87.8) * mm, "end": v(-640.8, 87.8) * mm});
            skLineSegment(sketch, "E312.MirrorCS", {"start": v(-592.88, -98.2) * mm, "end": v(-592.88, -102.2) * mm});
            skLineSegment(sketch, "E313.MirrorCS", {"start": v(-611.6, -98.2) * mm, "end": v(-611.6, -102.2) * mm});
            skLineSegment(sketch, "E314.MirrorCS", {"start": v(-630.3, -98.2) * mm, "end": v(-630.3, -102.2) * mm});
            skLineSegment(sketch, "E315.MirrorCS", {"start": v(-649.02, -98.2) * mm, "end": v(-649.02, -102.2) * mm});
            skLineSegment(sketch, "E316.MirrorCS", {"start": v(-667.74, -98.2) * mm, "end": v(-667.74, -102.2) * mm});
            skLineSegment(sketch, "E317.MirrorCS", {"start": v(-574.17, -102.2) * mm, "end": v(-574.17, -98.2) * mm});
            skLineSegment(sketch, "E318.MirrorCS", {"start": v(-574.17, -98.2) * mm, "end": v(-592.88, -98.2) * mm});
            skLineSegment(sketch, "E319.MirrorCS", {"start": v(-611.6, -98.2) * mm, "end": v(-630.3, -98.2) * mm});
            skLineSegment(sketch, "E320.MirrorCS", {"start": v(-611.6, -102.2) * mm, "end": v(-630.3, -102.2) * mm});
            skLineSegment(sketch, "E321.MirrorCS", {"start": v(-574.17, -102.2) * mm, "end": v(-592.88, -102.2) * mm});
            skLineSegment(sketch, "E322.MirrorCS", {"start": v(-649.02, -102.2) * mm, "end": v(-667.74, -102.2) * mm});
            skLineSegment(sketch, "E323.MirrorCS", {"start": v(-649.02, -98.2) * mm, "end": v(-667.74, -98.2) * mm});
            skLineSegment(sketch, "E324.MirrorCS", {"start": v(-563.3, -106.2) * mm, "end": v(-678.3, -106.2) * mm});
            skLineSegment(sketch, "E325", {"start": v(-600.8, 87.8) * mm, "end": v(-600.8, 91.8) * mm});
            skLineSegment(sketch, "E326", {"start": v(-640.8, 87.8) * mm, "end": v(-640.8, 91.8) * mm});
            skLineSegment(sketch, "E327.bottom", {"start": v(-1050.96, 230.69) * mm, "end": v(-1005.96, 230.69) * mm});
            skLineSegment(sketch, "E327.top", {"start": v(-1050.96, 115.69) * mm, "end": v(-1005.96, 115.69) * mm});
            skLineSegment(sketch, "E327.right", {"start": v(-920.96, 230.69) * mm, "end": v(-920.96, 193.19) * mm});
            skLineSegment(sketch, "E328.bottom", {"start": v(-1005.96, 234.69) * mm, "end": v(-965.96, 234.69) * mm});
            skLineSegment(sketch, "E328.left", {"start": v(-1005.96, 234.69) * mm, "end": v(-1005.96, 230.69) * mm});
            skLineSegment(sketch, "E328.right", {"start": v(-965.96, 234.69) * mm, "end": v(-965.96, 230.69) * mm});
            skLineSegment(sketch, "E329.trimOffspring", {"start": v(-965.96, 230.69) * mm, "end": v(-920.96, 230.69) * mm});
            skLineSegment(sketch, "E330.MirrorCS", {"start": v(-920.96, 153.19) * mm, "end": v(-916.96, 153.19) * mm});
            skLineSegment(sketch, "E331.MirrorCS", {"start": v(-916.96, 193.19) * mm, "end": v(-916.96, 153.19) * mm});
            skLineSegment(sketch, "E332.MirrorCS", {"start": v(-920.96, 193.19) * mm, "end": v(-916.96, 193.19) * mm});
            skLineSegment(sketch, "E333.MirrorCS", {"start": v(-965.96, 111.69) * mm, "end": v(-965.96, 115.69) * mm});
            skLineSegment(sketch, "E334.MirrorCS", {"start": v(-1005.96, 111.69) * mm, "end": v(-965.96, 111.69) * mm});
            skLineSegment(sketch, "E335.MirrorCS", {"start": v(-1005.96, 111.69) * mm, "end": v(-1005.96, 115.69) * mm});
            skLineSegment(sketch, "E336.trimOffspring", {"start": v(-920.96, 153.19) * mm, "end": v(-920.96, 115.69) * mm});
            skLineSegment(sketch, "E337.trimOffspring", {"start": v(-965.96, 115.69) * mm, "end": v(-920.96, 115.69) * mm});
            skLineSegment(sketch, "E338.MirrorCS", {"start": v(-1180.96, 193.19) * mm, "end": v(-1184.96, 193.19) * mm});
            skLineSegment(sketch, "E339.MirrorCS", {"start": v(-1180.96, 153.19) * mm, "end": v(-1184.96, 153.19) * mm});
            skLineSegment(sketch, "E340.MirrorCS", {"start": v(-1184.96, 193.19) * mm, "end": v(-1184.96, 153.19) * mm});
            skLineSegment(sketch, "E341.MirrorCS", {"start": v(-1180.96, 230.69) * mm, "end": v(-1180.96, 193.19) * mm});
            skLineSegment(sketch, "E342.MirrorCS", {"start": v(-1135.96, 115.69) * mm, "end": v(-1180.96, 115.69) * mm});
            skLineSegment(sketch, "E343.MirrorCS", {"start": v(-1135.96, 230.69) * mm, "end": v(-1180.96, 230.69) * mm});
            skLineSegment(sketch, "E344.MirrorCS", {"start": v(-1180.96, 153.19) * mm, "end": v(-1180.96, 115.69) * mm});
            skLineSegment(sketch, "E345.MirrorCS", {"start": v(-1095.96, 234.69) * mm, "end": v(-1095.96, 230.69) * mm});
            skLineSegment(sketch, "E346.MirrorCS", {"start": v(-1095.96, 234.69) * mm, "end": v(-1135.96, 234.69) * mm});
            skLineSegment(sketch, "E347.MirrorCS", {"start": v(-1050.96, 230.69) * mm, "end": v(-1095.96, 230.69) * mm});
            skLineSegment(sketch, "E348.MirrorCS", {"start": v(-1095.96, 111.69) * mm, "end": v(-1095.96, 115.69) * mm});
            skLineSegment(sketch, "E349.MirrorCS", {"start": v(-1095.96, 111.69) * mm, "end": v(-1135.96, 111.69) * mm});
            skLineSegment(sketch, "E350.MirrorCS", {"start": v(-1050.96, 115.69) * mm, "end": v(-1095.96, 115.69) * mm});
            skLineSegment(sketch, "E351", {"start": v(-1135.96, 111.69) * mm, "end": v(-1135.96, 115.69) * mm});
            skLineSegment(sketch, "E352", {"start": v(-1135.96, 230.69) * mm, "end": v(-1135.96, 234.69) * mm});
            skLineSegment(sketch, "E353.bottom", {"start": v(-827.88, -127.3) * mm, "end": v(-809.77, -127.3) * mm});
            skLineSegment(sketch, "E353.top", {"start": v(-827.88, -154.04) * mm, "end": v(-809.77, -154.04) * mm});
            skLineSegment(sketch, "E353.left", {"start": v(-827.88, -127.3) * mm, "end": v(-827.88, -154.04) * mm});
            skLineSegment(sketch, "E353.right", {"start": v(-809.77, -127.3) * mm, "end": v(-809.77, -154.04) * mm});
            skLineSegment(sketch, "E354.bottom", {"start": v(-134.23, 75.43) * mm, "end": v(-117.73, 75.43) * mm});
            skLineSegment(sketch, "E354.top", {"start": v(-134.23, 66.83) * mm, "end": v(-117.73, 66.83) * mm});
            skLineSegment(sketch, "E354.left", {"start": v(-134.23, 75.43) * mm, "end": v(-134.23, 66.83) * mm});
            skLineSegment(sketch, "E354.right", {"start": v(-117.73, 75.43) * mm, "end": v(-117.73, 66.83) * mm});
            skLineSegment(sketch, "E355", {"start": v(-125.98, 91.76) * mm, "end": v(-125.98, 36.36) * mm, "construction": true});
            skLineSegment(sketch, "E356.bottom", {"start": v(-939.63, 181.44) * mm, "end": v(-939.63, 164.94) * mm});
            skLineSegment(sketch, "E356.top", {"start": v(-948.23, 181.44) * mm, "end": v(-948.23, 164.94) * mm});
            skLineSegment(sketch, "E356.left", {"start": v(-939.63, 181.44) * mm, "end": v(-948.23, 181.44) * mm});
            skLineSegment(sketch, "E356.right", {"start": v(-939.63, 164.94) * mm, "end": v(-948.23, 164.94) * mm});
            skLineSegment(sketch, "E357.MirrorCS", {"start": v(-948.23, 164.94) * mm, "end": v(-948.23, 181.44) * mm});
            skLineSegment(sketch, "E358.MirrorCS", {"start": v(-939.63, 164.94) * mm, "end": v(-939.63, 181.44) * mm});
            skLineSegment(sketch, "E359", {"start": v(-1050.96, 230.69) * mm, "end": v(-1050.96, 115.69) * mm, "construction": true});
            skLineSegment(sketch, "E360.MirrorCS", {"start": v(-1153.7, 164.94) * mm, "end": v(-1153.7, 181.44) * mm});
            skLineSegment(sketch, "E361.MirrorCS", {"start": v(-1162.3, 164.94) * mm, "end": v(-1162.3, 181.44) * mm});
            skLineSegment(sketch, "E362.MirrorCS", {"start": v(-1162.3, 181.44) * mm, "end": v(-1153.7, 181.44) * mm});
            skLineSegment(sketch, "E363.MirrorCS", {"start": v(-1162.3, 164.94) * mm, "end": v(-1153.7, 164.94) * mm});
            skLineSegment(sketch, "E364.MirrorCS", {"start": v(-1162.3, 181.44) * mm, "end": v(-1162.3, 164.94) * mm});
            skLineSegment(sketch, "E365.MirrorCS", {"start": v(-1153.7, 181.44) * mm, "end": v(-1153.7, 164.94) * mm});
            skLineSegment(sketch, "E366.MirrorCS", {"start": v(-32.65, -347.05) * mm, "end": v(-28.65, -347.05) * mm});
            skLineSegment(sketch, "E367.MirrorCS", {"start": v(-32.65, -307.05) * mm, "end": v(-28.65, -307.05) * mm});
            skLineSegment(sketch, "E368.MirrorCS", {"start": v(-77.65, -388.55) * mm, "end": v(-77.65, -384.55) * mm});
            skLineSegment(sketch, "E369.MirrorCS", {"start": v(-162.65, -347.05) * mm, "end": v(-166.65, -347.05) * mm});
            skLineSegment(sketch, "E370.MirrorCS", {"start": v(-162.65, -307.05) * mm, "end": v(-166.65, -307.05) * mm});
            skLineSegment(sketch, "E371.MirrorCS", {"start": v(-117.65, -388.55) * mm, "end": v(-117.65, -384.55) * mm});
            skLineSegment(sketch, "E372.MirrorCS", {"start": v(-28.65, -347.05) * mm, "end": v(-28.65, -307.05) * mm});
            skLineSegment(sketch, "E373.MirrorCS", {"start": v(-162.65, -384.55) * mm, "end": v(-162.65, -347.05) * mm});
            skLineSegment(sketch, "E374.MirrorCS", {"start": v(-32.65, -307.05) * mm, "end": v(-32.65, -269.55) * mm});
            skLineSegment(sketch, "E375.MirrorCS", {"start": v(-32.65, -384.55) * mm, "end": v(-32.65, -347.05) * mm});
            skLineSegment(sketch, "E376.MirrorCS", {"start": v(-166.65, -347.05) * mm, "end": v(-166.65, -307.05) * mm});
            skLineSegment(sketch, "E377.MirrorCS", {"start": v(-117.65, -388.55) * mm, "end": v(-77.65, -388.55) * mm});
            skLineSegment(sketch, "E378.MirrorCS", {"start": v(-162.65, -307.05) * mm, "end": v(-162.65, -269.55) * mm});
            skLineSegment(sketch, "E379.MirrorCS", {"start": v(-162.65, -384.55) * mm, "end": v(-117.65, -384.55) * mm});
            skLineSegment(sketch, "E380.MirrorCS", {"start": v(-77.65, -384.55) * mm, "end": v(-32.65, -384.55) * mm});
            skLineSegment(sketch, "E381.bottom", {"start": v(-105.85, -174.08) * mm, "end": v(-89.45, -174.08) * mm});
            skLineSegment(sketch, "E381.top", {"start": v(-105.85, -182.48) * mm, "end": v(-89.45, -182.48) * mm});
            skLineSegment(sketch, "E381.left", {"start": v(-105.85, -174.08) * mm, "end": v(-105.85, -182.48) * mm});
            skLineSegment(sketch, "E381.right", {"start": v(-89.45, -174.08) * mm, "end": v(-89.45, -182.48) * mm});
            skPoint(sketch, "E382.startSnap0", {"position": v(-97.65, -174.08) * mm});
            skLineSegment(sketch, "E383.MirrorCS", {"start": v(-89.45, -365.02) * mm, "end": v(-89.45, -356.62) * mm});
            skLineSegment(sketch, "E384.MirrorCS", {"start": v(-105.85, -365.02) * mm, "end": v(-105.85, -356.62) * mm});
            skLineSegment(sketch, "E385.MirrorCS", {"start": v(-105.85, -356.62) * mm, "end": v(-89.45, -356.62) * mm});
            skLineSegment(sketch, "E386.MirrorCS", {"start": v(-105.85, -365.02) * mm, "end": v(-89.45, -365.02) * mm});
            skPoint(sketch, "E387.MirrorP", {"position": v(-97.65, -365.02) * mm});
            skLineSegment(sketch, "E388.bottom", {"start": v(113.8, -257.36) * mm, "end": v(158.8, -257.36) * mm});
            skLineSegment(sketch, "E388.right", {"start": v(243.8, -257.36) * mm, "end": v(243.8, -307.36) * mm});
            skLineSegment(sketch, "E389.bottom", {"start": v(158.8, -253.36) * mm, "end": v(198.8, -253.36) * mm});
            skLineSegment(sketch, "E389.left", {"start": v(158.8, -253.36) * mm, "end": v(158.8, -257.36) * mm});
            skLineSegment(sketch, "E389.right", {"start": v(198.8, -253.36) * mm, "end": v(198.8, -257.36) * mm});
            skLineSegment(sketch, "E390.trimOffspring", {"start": v(198.8, -257.36) * mm, "end": v(243.8, -257.36) * mm});
            skLineSegment(sketch, "E391.MirrorCS", {"start": v(243.8, -347.36) * mm, "end": v(247.8, -347.36) * mm});
            skLineSegment(sketch, "E392.MirrorCS", {"start": v(247.8, -307.36) * mm, "end": v(247.8, -347.36) * mm});
            skLineSegment(sketch, "E393.MirrorCS", {"start": v(243.8, -307.36) * mm, "end": v(247.8, -307.36) * mm});
            skLineSegment(sketch, "E394.bottom", {"start": v(170.6, -279.4) * mm, "end": v(187, -279.4) * mm});
            skLineSegment(sketch, "E394.top", {"start": v(170.6, -287.8) * mm, "end": v(187, -287.8) * mm});
            skLineSegment(sketch, "E394.left", {"start": v(170.6, -279.4) * mm, "end": v(170.6, -287.8) * mm});
            skLineSegment(sketch, "E394.right", {"start": v(187, -279.4) * mm, "end": v(187, -287.8) * mm});
            skPoint(sketch, "E395.startSnap0", {"position": v(178.8, -279.4) * mm});
            skPoint(sketch, "E396.orphan", {"position": v(276.7, 116.73) * mm});
            skLineSegment(sketch, "E397.1.0.0", {"start": v(157.54, 304.36) * mm, "end": v(161.54, 304.36) * mm});
            skLineSegment(sketch, "E397.2.0.0", {"start": v(157.54, 277.21) * mm, "end": v(161.54, 277.21) * mm});
            skLineSegment(sketch, "E397.3.0.0", {"start": v(157.54, 250.07) * mm, "end": v(161.54, 250.07) * mm});
            skLineSegment(sketch, "E397.4.0.0", {"start": v(157.54, 222.93) * mm, "end": v(161.54, 222.93) * mm});
            skLineSegment(sketch, "E397.5.0.0", {"start": v(157.54, 195.79) * mm, "end": v(161.54, 195.79) * mm});
            skLineSegment(sketch, "E397.6.0.0", {"start": v(157.54, 168.64) * mm, "end": v(161.54, 168.64) * mm});
            skLineSegment(sketch, "E398.0", {"start": v(161.54, 331.5) * mm, "end": v(161.54, 304.36) * mm});
            skLineSegment(sketch, "E399.trimOffspring", {"start": v(161.54, 277.21) * mm, "end": v(161.54, 250.07) * mm});
            skLineSegment(sketch, "E400.trimOffspring", {"start": v(161.54, 222.93) * mm, "end": v(161.54, 195.79) * mm});
            skLineSegment(sketch, "E401.trimOffspring", {"start": v(161.54, 168.64) * mm, "end": v(161.54, 133.5) * mm});
            skLineSegment(sketch, "E402", {"start": v(157.54, 168.64) * mm, "end": v(157.54, 195.79) * mm});
            skLineSegment(sketch, "E403", {"start": v(157.54, 222.93) * mm, "end": v(157.54, 250.07) * mm});
            skLineSegment(sketch, "E404", {"start": v(157.54, 277.21) * mm, "end": v(157.54, 304.36) * mm});
            skPoint(sketch, "E405.orphan", {"position": v(284.54, 133.5) * mm});
            skPoint(sketch, "E406.MirrorP", {"position": v(161.7, 116.73) * mm});
            skPoint(sketch, "E407.orphan", {"position": v(214.04, 339) * mm});
            skLineSegment(sketch, "E408", {"start": v(231.54, 111.63) * mm, "end": v(231.54, 342.52) * mm, "construction": true});
            skPoint(sketch, "E409.left.end.orphan", {"position": v(214.04, 327.5) * mm});
            skLineSegment(sketch, "E410", {"start": v(161.54, 331.5) * mm, "end": v(211.54, 331.5) * mm});
            skLineSegment(sketch, "E411.left", {"start": v(211.54, 331.5) * mm, "end": v(211.54, 327.5) * mm});
            skLineSegment(sketch, "E411.right", {"start": v(251.54, 331.5) * mm, "end": v(251.54, 327.5) * mm});
            skLineSegment(sketch, "E412.trimOffspring", {"start": v(251.54, 331.5) * mm, "end": v(301.54, 331.5) * mm});
            skLineSegment(sketch, "E413.trimOffspring", {"start": v(211.54, 327.5) * mm, "end": v(251.54, 327.5) * mm});
            skPoint(sketch, "E414.start.orphan", {"position": v(154.45, 327.5) * mm});
            skLineSegment(sketch, "E415.bottom", {"start": v(222.26, 141.24) * mm, "end": v(240.83, 141.24) * mm});
            skLineSegment(sketch, "E415.top", {"start": v(222.26, 137.5) * mm, "end": v(240.83, 137.5) * mm});
            skLineSegment(sketch, "E415.left", {"start": v(222.26, 141.24) * mm, "end": v(222.26, 137.5) * mm});
            skLineSegment(sketch, "E415.right", {"start": v(240.83, 141.24) * mm, "end": v(240.83, 137.5) * mm});
            skLineSegment(sketch, "E416.1.0.0", {"start": v(259.4, 141.24) * mm, "end": v(259.4, 137.5) * mm});
            skLineSegment(sketch, "E416.2.0.0", {"start": v(277.97, 141.24) * mm, "end": v(277.97, 137.5) * mm});
            skLineSegment(sketch, "E416.2.0.2", {"start": v(259.4, 137.5) * mm, "end": v(277.97, 137.5) * mm});
            skLineSegment(sketch, "E416.2.0.3", {"start": v(259.4, 141.24) * mm, "end": v(277.97, 141.24) * mm});
            skLineSegment(sketch, "E416.direction1", {"start": v(222.26, 137.5) * mm, "end": v(240.83, 137.5) * mm, "construction": true});
            skLineSegment(sketch, "E417.MirrorCS", {"start": v(203.69, 141.24) * mm, "end": v(185.12, 141.24) * mm});
            skLineSegment(sketch, "E418.MirrorCS", {"start": v(185.12, 141.24) * mm, "end": v(185.12, 137.5) * mm});
            skLineSegment(sketch, "E419.MirrorCS", {"start": v(203.69, 141.24) * mm, "end": v(203.69, 137.5) * mm});
            skLineSegment(sketch, "E420.MirrorCS", {"start": v(203.69, 137.5) * mm, "end": v(185.12, 137.5) * mm});
            skLineSegment(sketch, "E421.MirrorCS", {"start": v(305.54, 277.21) * mm, "end": v(301.54, 277.21) * mm});
            skLineSegment(sketch, "E422.MirrorCS", {"start": v(305.54, 250.07) * mm, "end": v(301.54, 250.07) * mm});
            skLineSegment(sketch, "E423.MirrorCS", {"start": v(305.54, 222.93) * mm, "end": v(301.54, 222.93) * mm});
            skLineSegment(sketch, "E424.MirrorCS", {"start": v(305.54, 304.36) * mm, "end": v(301.54, 304.36) * mm});
            skLineSegment(sketch, "E425.MirrorCS", {"start": v(305.54, 195.79) * mm, "end": v(301.54, 195.79) * mm});
            skLineSegment(sketch, "E426.MirrorCS", {"start": v(305.54, 168.64) * mm, "end": v(301.54, 168.64) * mm});
            skPoint(sketch, "E427.MirrorP", {"position": v(308.63, 327.5) * mm});
            skLineSegment(sketch, "E428.MirrorCS", {"start": v(305.54, 168.64) * mm, "end": v(305.54, 195.79) * mm});
            skLineSegment(sketch, "E429.MirrorCS", {"start": v(301.54, 168.64) * mm, "end": v(301.54, 133.5) * mm});
            skLineSegment(sketch, "E430.MirrorCS", {"start": v(301.54, 277.21) * mm, "end": v(301.54, 250.07) * mm});
            skLineSegment(sketch, "E431.MirrorCS", {"start": v(301.54, 331.5) * mm, "end": v(301.54, 304.36) * mm});
            skLineSegment(sketch, "E432.MirrorCS", {"start": v(305.54, 222.93) * mm, "end": v(305.54, 250.07) * mm});
            skLineSegment(sketch, "E433.MirrorCS", {"start": v(301.54, 222.93) * mm, "end": v(301.54, 195.79) * mm});
            skLineSegment(sketch, "E434.MirrorCS", {"start": v(305.54, 277.21) * mm, "end": v(305.54, 304.36) * mm});
            skLineSegment(sketch, "E435", {"start": v(161.54, 133.5) * mm, "end": v(301.54, 133.5) * mm});
            skLineSegment(sketch, "E436.MirrorCS", {"start": v(259.61, 91.77) * mm, "end": v(259.61, 87.77) * mm});
            skLineSegment(sketch, "E437.MirrorCS", {"start": v(184.75, 91.77) * mm, "end": v(184.75, 87.77) * mm});
            skLineSegment(sketch, "E438.MirrorCS", {"start": v(240.9, 91.77) * mm, "end": v(240.9, 87.77) * mm});
            skLineSegment(sketch, "E439.MirrorCS", {"start": v(222.18, 91.77) * mm, "end": v(222.18, 87.77) * mm});
            skLineSegment(sketch, "E440.MirrorCS", {"start": v(203.47, 91.77) * mm, "end": v(203.47, 87.77) * mm});
            skLineSegment(sketch, "E441.MirrorCS", {"start": v(278.33, 87.77) * mm, "end": v(278.33, 91.77) * mm});
            skLineSegment(sketch, "E442.MirrorCS", {"start": v(259.61, 87.77) * mm, "end": v(240.9, 87.77) * mm});
            skPoint(sketch, "E443.MirrorP", {"position": v(166.98, 87.97) * mm});
            skLineSegment(sketch, "E444.MirrorCS", {"start": v(222.18, 87.77) * mm, "end": v(203.47, 87.77) * mm});
            skLineSegment(sketch, "E445.MirrorCS", {"start": v(203.47, 91.77) * mm, "end": v(184.75, 91.77) * mm});
            skLineSegment(sketch, "E446.MirrorCS", {"start": v(278.33, 91.77) * mm, "end": v(259.61, 91.77) * mm});
            skLineSegment(sketch, "E447.MirrorCS", {"start": v(240.9, 91.77) * mm, "end": v(222.18, 91.77) * mm});
            skLineSegment(sketch, "E448.MirrorCS", {"start": v(184.75, -46.23) * mm, "end": v(184.75, -42.23) * mm});
            skLineSegment(sketch, "E449.MirrorCS", {"start": v(278.33, -42.23) * mm, "end": v(278.33, -46.23) * mm});
            skLineSegment(sketch, "E450.MirrorCS", {"start": v(203.47, -46.23) * mm, "end": v(203.47, -42.23) * mm});
            skLineSegment(sketch, "E451.MirrorCS", {"start": v(222.18, -46.23) * mm, "end": v(222.18, -42.23) * mm});
            skLineSegment(sketch, "E452.MirrorCS", {"start": v(240.9, -46.23) * mm, "end": v(240.9, -42.23) * mm});
            skLineSegment(sketch, "E453.MirrorCS", {"start": v(259.61, -46.23) * mm, "end": v(259.61, -42.23) * mm});
            skPoint(sketch, "E454.MirrorP", {"position": v(186.36, -23.66) * mm});
            skLineSegment(sketch, "E455.MirrorCS", {"start": v(240.9, -46.23) * mm, "end": v(222.18, -46.23) * mm});
            skLineSegment(sketch, "E456.MirrorCS", {"start": v(278.33, -46.23) * mm, "end": v(259.61, -46.23) * mm});
            skLineSegment(sketch, "E457.MirrorCS", {"start": v(222.18, -42.23) * mm, "end": v(203.47, -42.23) * mm});
            skLineSegment(sketch, "E458.MirrorCS", {"start": v(259.61, -42.23) * mm, "end": v(240.9, -42.23) * mm});
            skLineSegment(sketch, "E459.MirrorCS", {"start": v(203.47, -46.23) * mm, "end": v(184.75, -46.23) * mm});
            skLineSegment(sketch, "E460.MirrorCS", {"start": v(161.54, -5.1) * mm, "end": v(157.54, -5.1) * mm});
            skLineSegment(sketch, "E461.MirrorCS", {"start": v(161.54, 50.62) * mm, "end": v(157.54, 50.62) * mm});
            skLineSegment(sketch, "E462.MirrorCS", {"start": v(161.54, 13.48) * mm, "end": v(157.54, 13.48) * mm});
            skLineSegment(sketch, "E463.MirrorCS", {"start": v(161.54, 69.2) * mm, "end": v(157.54, 69.19) * mm});
            skLineSegment(sketch, "E464.MirrorCS", {"start": v(161.54, -23.66) * mm, "end": v(157.54, -23.67) * mm});
            skLineSegment(sketch, "E465.MirrorCS", {"start": v(161.54, 32.05) * mm, "end": v(157.54, 32.05) * mm});
            skLineSegment(sketch, "E466.MirrorCS", {"start": v(161.54, 50.62) * mm, "end": v(161.54, 32.05) * mm});
            skPoint(sketch, "E467.MirrorP", {"position": v(186.23, -5.09) * mm});
            skLineSegment(sketch, "E468.MirrorCS", {"start": v(161.54, 13.48) * mm, "end": v(161.54, -5.1) * mm});
            skLineSegment(sketch, "E469.MirrorCS", {"start": v(157.54, -5.1) * mm, "end": v(157.54, -23.67) * mm});
            skLineSegment(sketch, "E470.MirrorCS", {"start": v(161.54, -23.66) * mm, "end": v(161.54, -42.34) * mm});
            skLineSegment(sketch, "E471.MirrorCS", {"start": v(157.54, 32.05) * mm, "end": v(157.54, 13.48) * mm});
            skLineSegment(sketch, "E472.MirrorCS", {"start": v(157.54, 69.19) * mm, "end": v(157.54, 50.62) * mm});
            skLineSegment(sketch, "E473.MirrorCS", {"start": v(161.54, 87.88) * mm, "end": v(161.54, 69.2) * mm});
            skPoint(sketch, "E474.MirrorP", {"position": v(185.97, 32.06) * mm});
            skPoint(sketch, "E475.MirrorP", {"position": v(166.98, -53.07) * mm});
            skPoint(sketch, "E476.MirrorP", {"position": v(186.1, 13.49) * mm});
            skPoint(sketch, "E477.orphan", {"position": v(183.33, 94.29) * mm});
            skPoint(sketch, "E478.endSnap0", {"position": v(231.54, 91.77) * mm});
            skLineSegment(sketch, "E479", {"start": v(231.54, 91.77) * mm, "end": v(231.54, -46.23) * mm});
            skLineSegment(sketch, "E480", {"start": v(184.75, 87.77) * mm, "end": v(161.54, 87.88) * mm});
            skLineSegment(sketch, "E481", {"start": v(184.75, -42.23) * mm, "end": v(161.54, -42.34) * mm});
            skLineSegment(sketch, "E482.MirrorCS", {"start": v(301.54, -23.66) * mm, "end": v(305.54, -23.67) * mm});
            skLineSegment(sketch, "E483.MirrorCS", {"start": v(301.54, 32.05) * mm, "end": v(305.54, 32.05) * mm});
            skLineSegment(sketch, "E484.MirrorCS", {"start": v(301.54, -5.1) * mm, "end": v(305.54, -5.1) * mm});
            skLineSegment(sketch, "E485.MirrorCS", {"start": v(301.54, 50.62) * mm, "end": v(305.54, 50.62) * mm});
            skLineSegment(sketch, "E486.MirrorCS", {"start": v(301.54, 69.2) * mm, "end": v(305.54, 69.19) * mm});
            skLineSegment(sketch, "E487.MirrorCS", {"start": v(301.54, 13.48) * mm, "end": v(305.54, 13.48) * mm});
            skPoint(sketch, "E488.MirrorP", {"position": v(296.1, 87.97) * mm});
            skLineSegment(sketch, "E489.MirrorCS", {"start": v(305.54, 69.19) * mm, "end": v(305.54, 50.62) * mm});
            skLineSegment(sketch, "E490.MirrorCS", {"start": v(305.54, 32.05) * mm, "end": v(305.54, 13.48) * mm});
            skLineSegment(sketch, "E491.MirrorCS", {"start": v(305.54, -5.1) * mm, "end": v(305.54, -23.67) * mm});
            skLineSegment(sketch, "E492.MirrorCS", {"start": v(301.54, 13.48) * mm, "end": v(301.54, -5.1) * mm});
            skLineSegment(sketch, "E493.MirrorCS", {"start": v(301.54, 87.88) * mm, "end": v(301.54, 69.2) * mm});
            skLineSegment(sketch, "E494.MirrorCS", {"start": v(301.54, 50.62) * mm, "end": v(301.54, 32.05) * mm});
            skLineSegment(sketch, "E495.MirrorCS", {"start": v(301.54, -23.66) * mm, "end": v(301.54, -42.34) * mm});
            skLineSegment(sketch, "E496", {"start": v(278.33, 87.77) * mm, "end": v(301.54, 87.88) * mm});
            skLineSegment(sketch, "E497", {"start": v(278.33, -42.23) * mm, "end": v(301.54, -42.34) * mm});
            skLineSegment(sketch, "E498", {"start": v(243.8, -347.36) * mm, "end": v(243.8, -397.36) * mm});
            skLineSegment(sketch, "E499.MirrorCS", {"start": v(158.8, -401.36) * mm, "end": v(158.8, -397.36) * mm});
            skLineSegment(sketch, "E500.MirrorCS", {"start": v(198.8, -401.36) * mm, "end": v(198.8, -397.36) * mm});
            skLineSegment(sketch, "E501.MirrorCS", {"start": v(158.8, -401.36) * mm, "end": v(198.8, -401.36) * mm});
            skLineSegment(sketch, "E502.MirrorCS", {"start": v(198.8, -397.36) * mm, "end": v(243.8, -397.36) * mm});
            skLineSegment(sketch, "E503.MirrorCS", {"start": v(113.8, -397.36) * mm, "end": v(158.8, -397.36) * mm});
            skLineSegment(sketch, "E504.MirrorCS", {"start": v(113.8, -307.36) * mm, "end": v(109.8, -307.36) * mm});
            skLineSegment(sketch, "E505.MirrorCS", {"start": v(113.8, -347.36) * mm, "end": v(109.8, -347.36) * mm});
            skLineSegment(sketch, "E506.MirrorCS", {"start": v(113.8, -347.36) * mm, "end": v(113.8, -397.36) * mm});
            skLineSegment(sketch, "E507.MirrorCS", {"start": v(109.8, -307.36) * mm, "end": v(109.8, -347.36) * mm});
            skLineSegment(sketch, "E508.MirrorCS", {"start": v(113.8, -257.36) * mm, "end": v(113.8, -307.36) * mm});
            skSolve(sketch);
        }
        {
            var Q0;
            Q0 = qSketchRegion(id + "F0", true);
            extrude(context, id + "F1", {"entities" : qUnion([Q0]), "depth" : 4 * mm});
        }
    });
